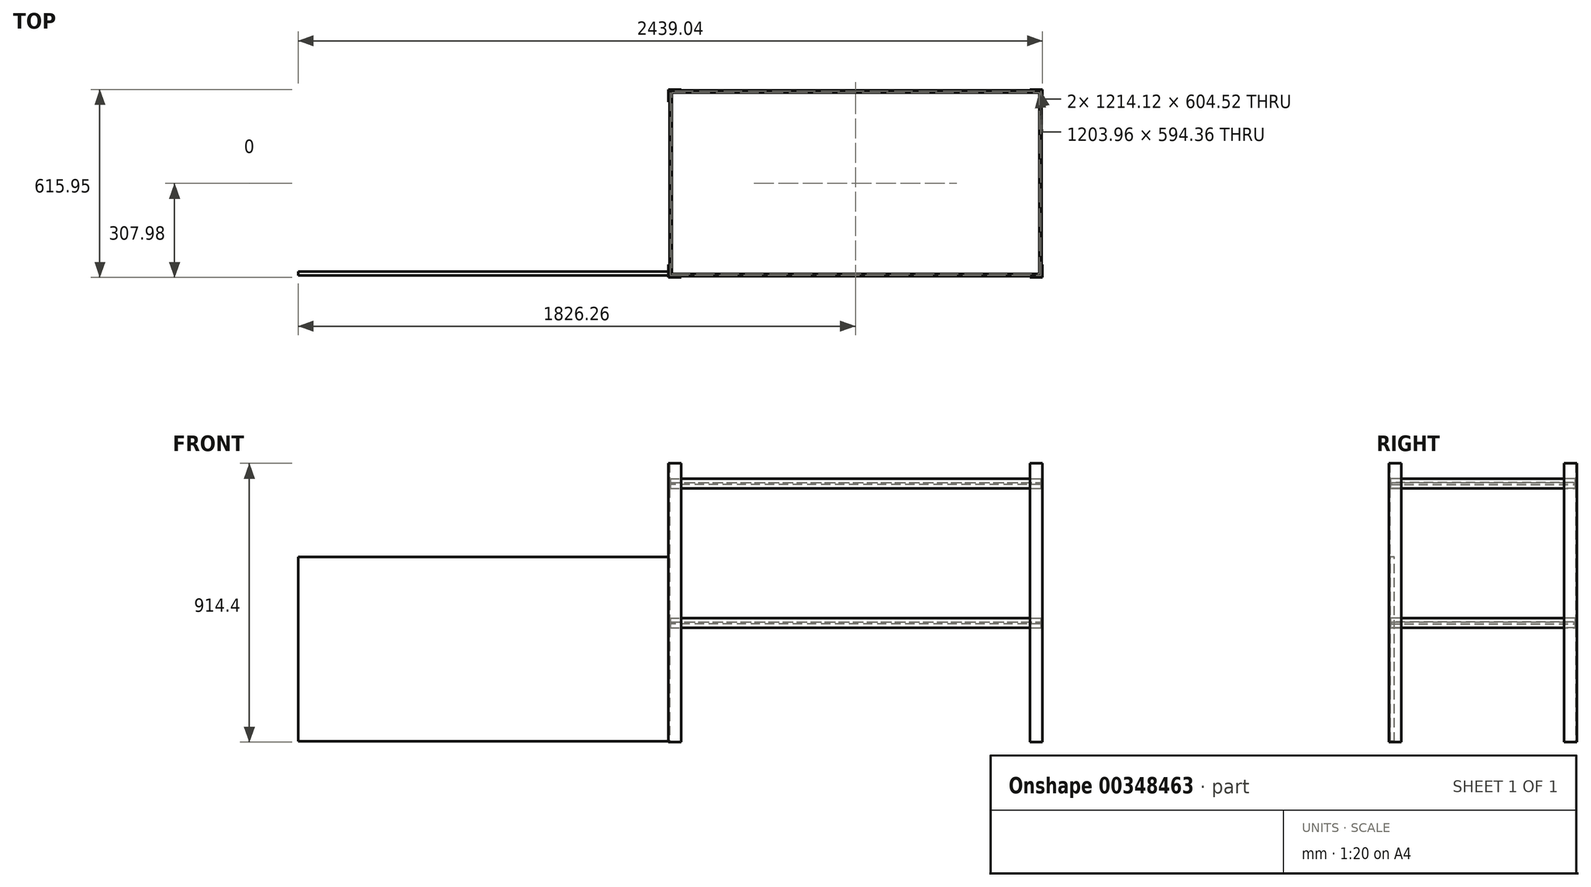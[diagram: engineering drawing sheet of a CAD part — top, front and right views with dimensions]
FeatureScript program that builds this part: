
annotation { "Feature Type Name" : "Feature", "Feature Type Description" : "" }
export const myFeature = defineFeature(function(context is Context, id is Id, definition is map)
    precondition{}
    {
        {
            var Q0;
            Q0=qCreatedBy(makeId("Top.planeOp"),FACE);
            var sketch = newSketch(context, id + "F0", { "sketchPlane" : qUnion([Q0])});
            skLineSegment(sketch, "E0", {"start": v(-3.18, 38.1) * mm, "end": v(0, 38.1) * mm});
            skLineSegment(sketch, "E1", {"start": v(-3.18, 38.1) * mm, "end": v(-3.17, -3.18) * mm});
            skLineSegment(sketch, "E2", {"start": v(-3.17, -3.18) * mm, "end": v(38.1, -3.18) * mm});
            skLineSegment(sketch, "E3", {"start": v(38.1, 0) * mm, "end": v(38.1, -3.18) * mm});
            skLineSegment(sketch, "E4", {"start": v(38.1, 0) * mm, "end": v(0, 0) * mm});
            skLineSegment(sketch, "E5", {"start": v(0, 0) * mm, "end": v(0, 38.1) * mm});
            skSolve(sketch);
        }
        {
            var Q0;
            Q0 = qSketchRegion(id + "F0", true);
            extrude(context, id + "F1", {"entities" : qUnion([Q0]), "depth" : 914.4 * mm});
        }
        {
            var Q0;
            Q0=qCreatedBy(makeId("Right.planeOp"),FACE);
            cPlane(context, id + "F2", {"entities" : qUnion([Q0]), "cplaneType" : CPlaneType.OFFSET, "offset" : 609.6 * mm, "width" : 152.4 * mm, "height" : 152.4 * mm});
        }
        {
            var Q0;
            Q0=qCreatedBy(makeId("Front.planeOp"),FACE);
            cPlane(context, id + "F3", {"entities" : qUnion([Q0]), "cplaneType" : CPlaneType.OFFSET, "offset" : 304.8 * mm, "oppositeDirection" : true, "width" : 152.4 * mm, "height" : 152.4 * mm});
        }
        {
            var Q0;
            Q0=makeQuery(id+"F1.opExtrude","SWEPT_BODY",BODY,{"disambiguationData":[OSD([sQuery(id+"F0.wireOp",EDGE,"E0"),sQuery(id+"F0.wireOp",EDGE,"E1"),sQuery(id+"F0.wireOp",EDGE,"E2"),sQuery(id+"F0.wireOp",EDGE,"E3"),sQuery(id+"F0.wireOp",EDGE,"E4"),sQuery(id+"F0.wireOp",EDGE,"E5")])]});
            var Q1;
            Q1=qCreatedBy(id+"F2.planeOp",FACE);
            mirror(context, id + "F4", {"entities" : qUnion([Q0]), "mirrorPlane" : qUnion([Q1])});
        }
        {
            var Q0;
            Q0=makeQuery(id+"F4.opPattern","COPY",BODY,{"derivedFrom":makeQuery(id+"F1.opExtrude","SWEPT_BODY",BODY,{"disambiguationData":[OSD([sQuery(id+"F0.wireOp",EDGE,"E0"),sQuery(id+"F0.wireOp",EDGE,"E1"),sQuery(id+"F0.wireOp",EDGE,"E2"),sQuery(id+"F0.wireOp",EDGE,"E3"),sQuery(id+"F0.wireOp",EDGE,"E4"),sQuery(id+"F0.wireOp",EDGE,"E5")])]}),"instanceName":"1"});
            var Q1;
            Q1=makeQuery(id+"F1.opExtrude","SWEPT_BODY",BODY,{"disambiguationData":[OSD([sQuery(id+"F0.wireOp",EDGE,"E0"),sQuery(id+"F0.wireOp",EDGE,"E1"),sQuery(id+"F0.wireOp",EDGE,"E2"),sQuery(id+"F0.wireOp",EDGE,"E3"),sQuery(id+"F0.wireOp",EDGE,"E4"),sQuery(id+"F0.wireOp",EDGE,"E5")])]});
            var Q2;
            Q2=qCreatedBy(id+"F3.planeOp",FACE);
            mirror(context, id + "F5", {"entities" : qUnion([Q0, Q1]), "mirrorPlane" : qUnion([Q2])});
        }
        {
            var Q0;
            Q0=qCreatedBy(makeId("Top.planeOp"),FACE);
            cPlane(context, id + "F6", {"entities" : qUnion([Q0]), "cplaneType" : CPlaneType.OFFSET, "offset" : 889 * mm, "width" : 152.4 * mm, "height" : 152.4 * mm});
        }
        {
            var Q0;
            Q0=qCreatedBy(id+"F6.planeOp",FACE);
            var sketch = newSketch(context, id + "F7", { "sketchPlane" : qUnion([Q0])});
            skLineSegment(sketch, "E6.bottom", {"start": v(1219.2, 609.6) * mm, "end": v(0, 609.6) * mm});
            skLineSegment(sketch, "E6.top", {"start": v(1219.2, 0) * mm, "end": v(0, 0) * mm});
            skLineSegment(sketch, "E6.left", {"start": v(1219.2, 609.6) * mm, "end": v(1219.2, 0) * mm});
            skLineSegment(sketch, "E6.right", {"start": v(0, 609.6) * mm, "end": v(0, 0) * mm});
            skSolve(sketch);
        }
        {
            var Q0;
            Q0=makeQuery(id+"F1.opExtrude","SWEPT_FACE",FACE,{"disambiguationData":[OSD([sQuery(id+"F0.wireOp",EDGE,"E3")])]});
            var sketch = newSketch(context, id + "F8", { "sketchPlane" : qUnion([Q0])});
            skLineSegment(sketch, "E7", {"start": v(0, 863.6) * mm, "end": v(0, 831.85) * mm});
            skLineSegment(sketch, "E8", {"start": v(0, 831.85) * mm, "end": v(2.54, 831.85) * mm});
            skLineSegment(sketch, "E9", {"start": v(2.54, 831.85) * mm, "end": v(2.54, 844.55) * mm});
            skLineSegment(sketch, "E10", {"start": v(2.54, 844.55) * mm, "end": v(7.62, 850.9) * mm});
            skLineSegment(sketch, "E11", {"start": v(7.62, 850.9) * mm, "end": v(2.54, 850.9) * mm});
            skLineSegment(sketch, "E12", {"start": v(2.54, 850.9) * mm, "end": v(2.54, 863.6) * mm});
            skLineSegment(sketch, "E13", {"start": v(2.54, 863.6) * mm, "end": v(0, 863.6) * mm});
            skLineSegment(sketch, "E14", {"start": v(0, 406.4) * mm, "end": v(0, 374.65) * mm});
            skLineSegment(sketch, "E15", {"start": v(0, 374.65) * mm, "end": v(2.54, 374.65) * mm});
            skLineSegment(sketch, "E16", {"start": v(2.54, 374.65) * mm, "end": v(2.54, 387.35) * mm});
            skLineSegment(sketch, "E17", {"start": v(2.54, 387.35) * mm, "end": v(7.62, 393.7) * mm});
            skLineSegment(sketch, "E18", {"start": v(7.62, 393.7) * mm, "end": v(2.54, 393.7) * mm});
            skLineSegment(sketch, "E19", {"start": v(2.54, 393.7) * mm, "end": v(2.54, 406.4) * mm});
            skLineSegment(sketch, "E20", {"start": v(2.54, 406.4) * mm, "end": v(0, 406.4) * mm});
            skSolve(sketch);
        }
        {
            var Q0;
            Q0 = qSketchRegion(id + "F8", true);
            var Q1;
            Q1=sQuery(id+"F7.wireOp",EDGE,"E6.top");
            var Q2;
            Q2=sQuery(id+"F7.wireOp",EDGE,"E6.left");
            var Q3;
            Q3=sQuery(id+"F7.wireOp",EDGE,"E6.bottom");
            var Q4;
            Q4=sQuery(id+"F7.wireOp",EDGE,"E6.right");
            sweep(context, id + "F9", {"operationType" : NewBodyOperationType.ADD, "profiles" : qUnion([Q0]), "path" : qUnion([Q1, Q2, Q3, Q4])});
        }
        {
            var Q0;
            Q0=makeQuery(id+"F9.opSweep","SWEPT_FACE",FACE,{"disambiguationData":[OSD([sQuery(id+"F7.wireOp",EDGE,"E6.top"),sQuery(id+"F8.wireOp",EDGE,"E11")])]});
            var sketch = newSketch(context, id + "F10", { "sketchPlane" : qUnion([Q0])});
            skLineSegment(sketch, "E21.bottom", {"start": v(2.54, 607.06) * mm, "end": v(1216.66, 607.06) * mm});
            skLineSegment(sketch, "E21.top", {"start": v(2.54, 2.54) * mm, "end": v(1216.66, 2.54) * mm});
            skLineSegment(sketch, "E21.left", {"start": v(2.54, 607.06) * mm, "end": v(2.54, 2.54) * mm});
            skLineSegment(sketch, "E21.right", {"start": v(1216.66, 607.06) * mm, "end": v(1216.66, 2.54) * mm});
            skSolve(sketch);
        }
        {
            var Q0;
            Q0 = qSketchRegion(id + "F10", true);
            extrude(context, id + "F11", {"entities" : qUnion([Q0]), "operationType" : NewBodyOperationType.ADD, "depth" : 12.7 * mm});
        }
        {
            var Q0;
            Q0=makeQuery(id+"F9.opSweep","SWEPT_FACE",FACE,{"disambiguationData":[OSD([sQuery(id+"F7.wireOp",EDGE,"E6.top"),sQuery(id+"F8.wireOp",EDGE,"E18")])]});
            var sketch = newSketch(context, id + "F12", { "sketchPlane" : qUnion([Q0])});
            skLineSegment(sketch, "E22.bottom", {"start": v(2.54, 607.06) * mm, "end": v(1216.66, 607.06) * mm});
            skLineSegment(sketch, "E22.top", {"start": v(2.54, 2.54) * mm, "end": v(1216.66, 2.54) * mm});
            skLineSegment(sketch, "E22.left", {"start": v(2.54, 607.06) * mm, "end": v(2.54, 2.54) * mm});
            skLineSegment(sketch, "E22.right", {"start": v(1216.66, 607.06) * mm, "end": v(1216.66, 2.54) * mm});
            skSolve(sketch);
        }
        {
            var Q0;
            Q0 = qSketchRegion(id + "F12", true);
            extrude(context, id + "F13", {"entities" : qUnion([Q0]), "operationType" : NewBodyOperationType.ADD, "depth" : 12.7 * mm});
        }
    });
